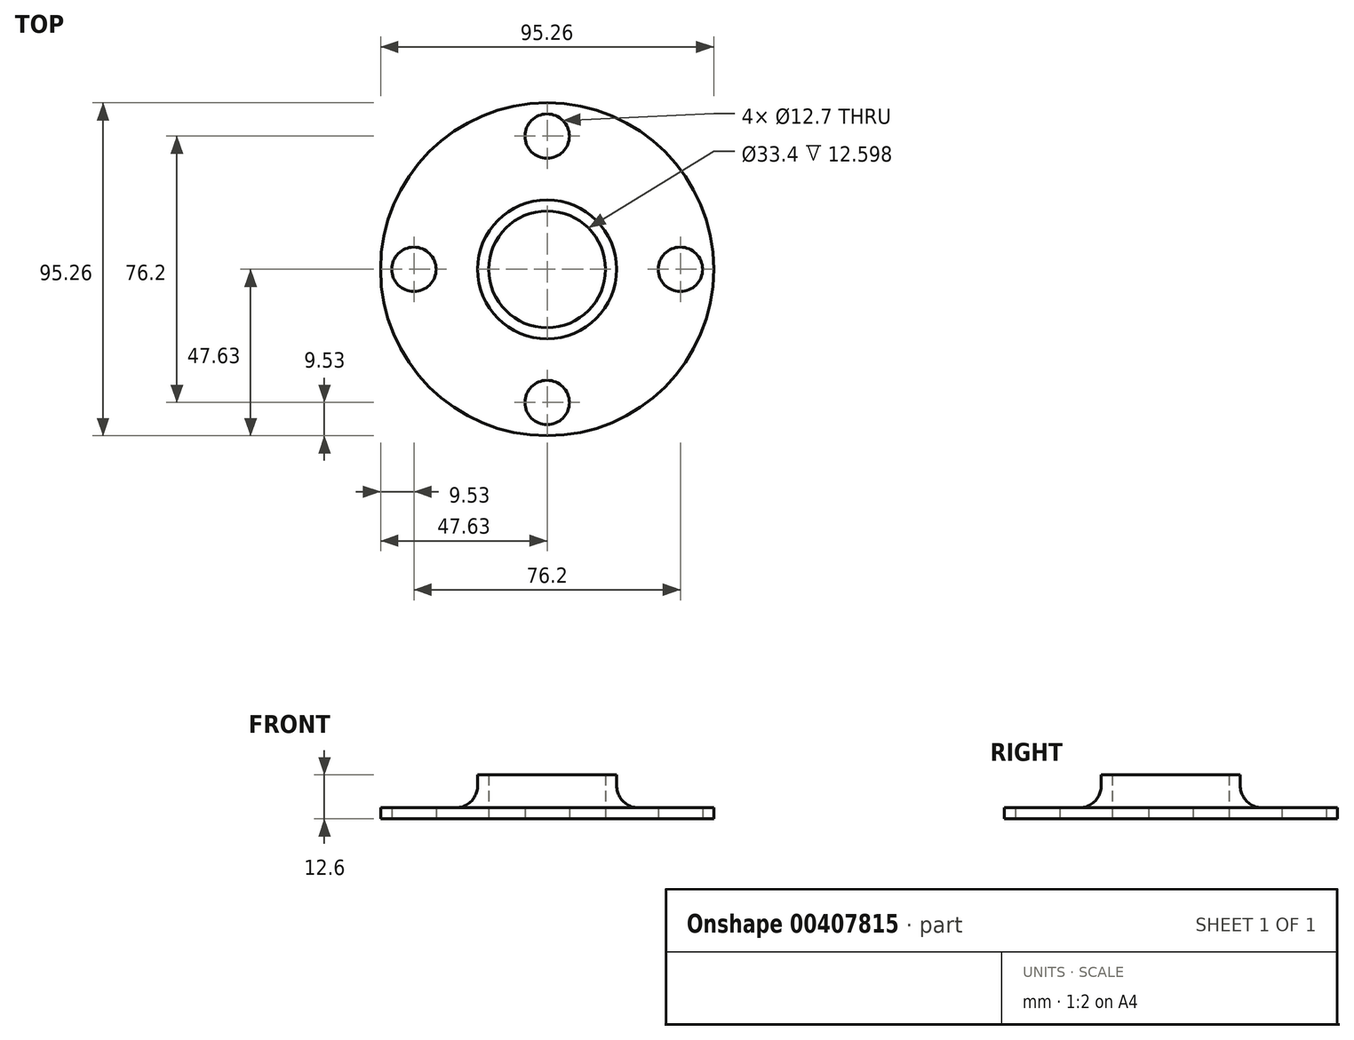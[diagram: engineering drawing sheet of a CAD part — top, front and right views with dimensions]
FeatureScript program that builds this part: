
annotation { "Feature Type Name" : "Feature", "Feature Type Description" : "" }
export const myFeature = defineFeature(function(context is Context, id is Id, definition is map)
    precondition{}
    {
        {
            var Q0;
            Q0=qCreatedBy(makeId("Top.planeOp"),FACE);
            var sketch = newSketch(context, id + "F0", { "sketchPlane" : qUnion([Q0])});
            skCircle(sketch, "E0", {"center": v(0, 0) * mm, "radius": 47.63 * mm});
            skCircle(sketch, "E1", {"center": v(0, 0) * mm, "radius": 16.7 * mm});
            skSolve(sketch);
        }
        {
            var Q0;
            Q0 = qSketchRegion(id + "F0", true);
            extrude(context, id + "F1", {"entities" : qUnion([Q0]), "depth" : 12.6 * mm});
        }
        {
            var Q0;
            Q0=qCreatedBy(makeId("Front.planeOp"),FACE);
            var sketch = newSketch(context, id + "F2", { "sketchPlane" : qUnion([Q0])});
            skLineSegment(sketch, "E2", {"start": v(50.8, 12.6) * mm, "end": v(19.88, 12.6) * mm});
            skLineSegment(sketch, "E3", {"start": v(50.8, 12.6) * mm, "end": v(50.8, 3.18) * mm});
            skLineSegment(sketch, "E4", {"start": v(0, 0) * mm, "end": v(0, 12.6) * mm, "construction": true});
            skLineSegment(sketch, "E5", {"start": v(19.88, 12.6) * mm, "end": v(19.88, 9.53) * mm});
            skLineSegment(sketch, "E6", {"start": v(26.23, 3.18) * mm, "end": v(50.8, 3.18) * mm});
            skPoint(sketch, "E7.visualSharp", {"position": v(19.88, 3.18) * mm});
            skArc(sketch, "E7.filletArc", {"start": v(19.88, 9.52) * mm, "mid": v(21.74, 5.03) * mm, "end": v(26.23, 3.18) * mm});
            skSolve(sketch);
        }
        {
            var Q0;
            Q0 = qSketchRegion(id + "F2", true);
            var Q1;
            Q1=sQuery(id+"F2.wireOp",EDGE,"E4");
            revolve(context, id + "F3", {"operationType" : NewBodyOperationType.REMOVE, "entities" : qUnion([Q0]), "axis" : qUnion([Q1]), "revolveType" : RevolveType.FULL, "oppositeDirection" : true});
        }
        {
            var Q0;
            Q0=makeQuery(id+"F1.opExtrude","CAP_FACE",FACE,{"disambiguationData":[OSD([sQuery(id+"F0.wireOp",EDGE,"E0"),sQuery(id+"F0.wireOp",EDGE,"E1")])],"isStart":true});
            var sketch = newSketch(context, id + "F4", { "sketchPlane" : qUnion([Q0])});
            skCircle(sketch, "E8", {"center": v(0, 38.1) * mm, "radius": 6.35 * mm});
            skCircle(sketch, "E9", {"center": v(0, -38.1) * mm, "radius": 6.35 * mm});
            skCircle(sketch, "E10", {"center": v(-38.1, 0) * mm, "radius": 6.35 * mm});
            skCircle(sketch, "E11", {"center": v(38.1, 0) * mm, "radius": 6.35 * mm});
            skSolve(sketch);
        }
        {
            var Q0;
            Q0 = qSketchRegion(id + "F4", true);
            extrude(context, id + "F5", {"entities" : qUnion([Q0]), "operationType" : NewBodyOperationType.REMOVE, "endBound" : BoundingType.THROUGH_ALL, "oppositeDirection" : true, "depth" : 25.4 * mm});
        }
    });
